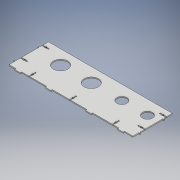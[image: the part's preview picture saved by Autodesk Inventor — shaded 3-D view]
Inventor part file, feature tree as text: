
AUTODESK INVENTOR PART (.ipt)
format: ipt  version: 2018 (Build 220112000, 112)  size: 428,544 bytes
history: native  units: mm
features: extrude x5, sketch x5, plane x3, projected_geometry x3, mirror x2
ambient origin geometry x8: Origin, YZ Plane, XZ Plane, XY Plane, X Axis, Y Axis, Z Axis, Center Point
bodies: Solid1 (feature_tree)
feature tree (18):
  extrude  "Extrusion1"  Depth=4.0mm
  sketch  "Sketch2"  dims[d3=27.0mm d4=3.6mm]
  plane  "Work Plane2"
  extrude  "Extrusion3"  Depth=3.6mm
  plane  "Work Plane3"
  mirror  "Mirror2"
  extrude  "Extrusion4"  Depth=6.0mm
  plane  "Work Plane4"
  mirror  "Mirror3"
  extrude  "Extrusion5"  Depth=140.0mm
  extrude  "Extrusion6"  Depth=27.0mm
  sketch  "Sketch1"  dims[d0=4.0mm d1=0.0mm d2=4.0mm]
  projected_geometry  "Projected Loop1"
  sketch  "Sketch3"  dims[d5=3.0mm d6=6.0mm]
  projected_geometry  "Projected Loop2"
  sketch  "Sketch4"  dims[d7=10.0mm d8=140.0mm]
  projected_geometry  "Projected Loop3"
  sketch  "Sketch5"  dims[d9=20.0mm d15=27.0mm d17=3.0mm d18=6.0mm d22=40.0mm d23=3.6mm d24=4.0mm d25=0.0mm d26=4.0mm d27=4.0mm d28=4.0mm d29=4.0mm d30=20.0mm d31=30.0mm d32=4.0mm d33=0.0mm d34=70.0mm d35=3.6mm d36=3.6mm d37=6.0mm d38=1.2mm d39=3.0mm d40=1.2mm d41=3.6mm d42=3.6mm d43=6.0mm d44=1.2mm d45=3.0mm d46=1.2mm d47=3.6mm d48=3.6mm d49=6.0mm d50=1.2mm d51=3.0mm d52=1.2mm d53=70.0mm d54=440.0mm d55=221.8mm d56=10.0mm d57=0.0mm d58=20.0mm d59=5.0mm d60=20.0mm d61=5.0mm d62=20.0mm d63=5.0mm d64=20.0mm d65=5.0mm d66=25.0mm d67=60.5mm d68=141.0mm d69=148.2mm d70=4.0mm d71=0.0mm]
